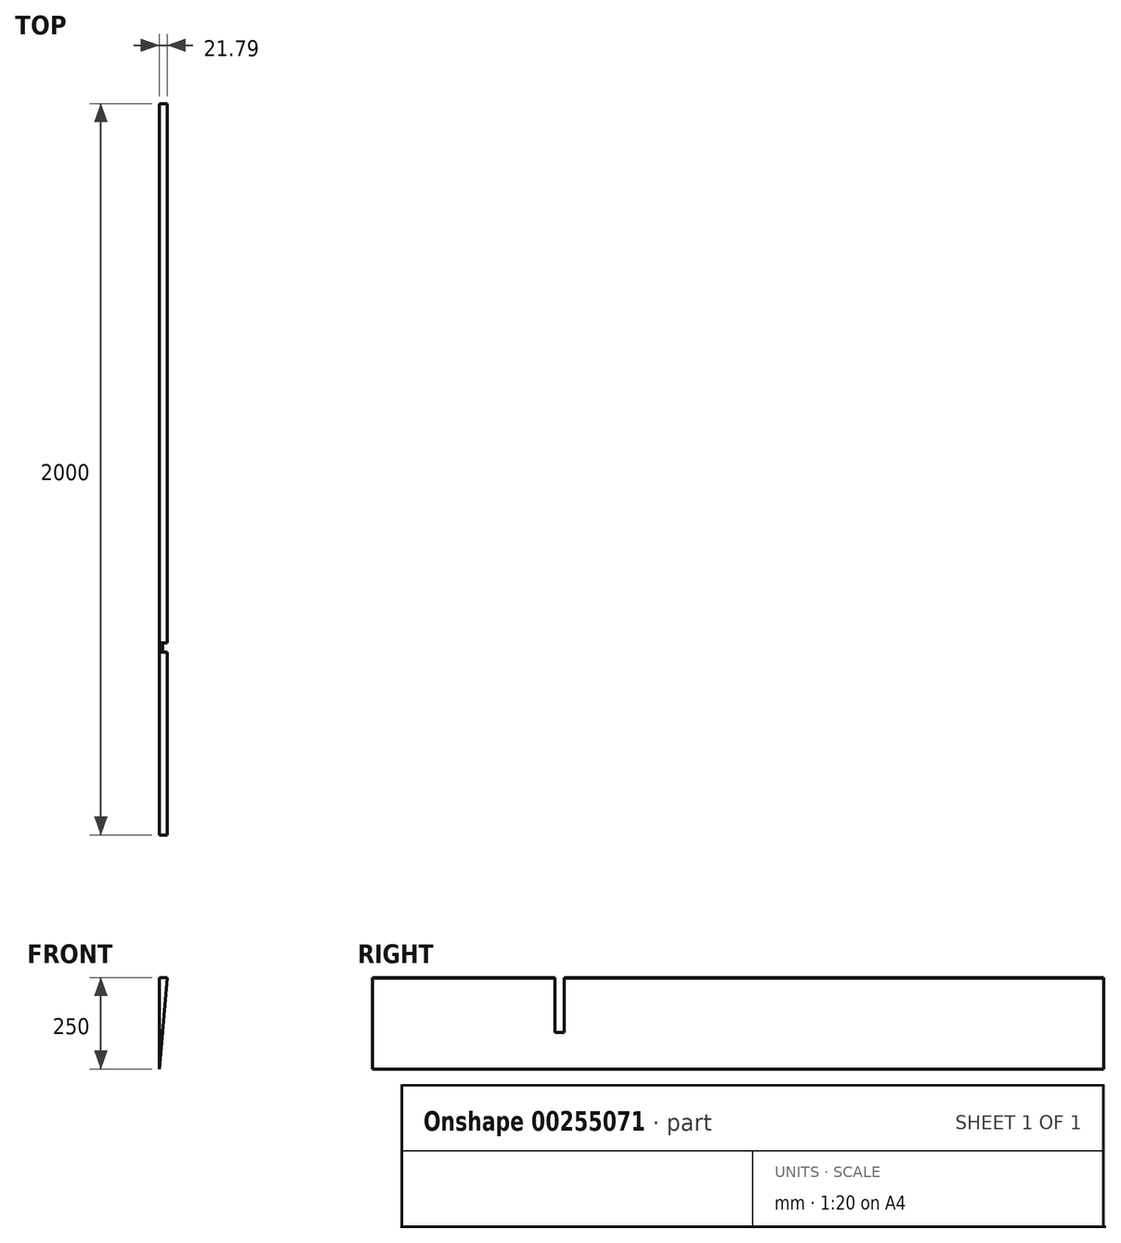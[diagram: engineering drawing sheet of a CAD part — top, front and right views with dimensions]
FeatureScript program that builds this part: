
annotation { "Feature Type Name" : "Feature", "Feature Type Description" : "" }
export const myFeature = defineFeature(function(context is Context, id is Id, definition is map)
    precondition{}
    {
        {
            var Q0;
            Q0=qCreatedBy(makeId("Front.planeOp"),FACE);
            var sketch = newSketch(context, id + "F0", { "sketchPlane" : qUnion([Q0])});
            skCircle(sketch, "E0", {"center": v(0, 0) * mm, "radius": 250 * mm});
            skSolve(sketch);
        }
        {
            var Q0;
            Q0=makeQuery(id+"F0.imprint","IMPRINT",FACE,{"disambiguationData":[TD([[makeQuery(id+"F0.imprint","IMPRINT",EDGE,{"derivedFrom":sQuery(id+"F0.wireOp",EDGE,"E0")}),1.0]])]});
            var sketch = newSketch(context, id + "F1", { "sketchPlane" : qUnion([Q0])});
            skLineSegment(sketch, "E1.bottom", {"start": v(100, -100) * mm, "end": v(-100, -100) * mm});
            skLineSegment(sketch, "E1.top", {"start": v(100, 100) * mm, "end": v(-100, 100) * mm});
            skLineSegment(sketch, "E1.left", {"start": v(100, -100) * mm, "end": v(100, 100) * mm});
            skLineSegment(sketch, "E1.right", {"start": v(-100, -100) * mm, "end": v(-100, 100) * mm});
            skPoint(sketch, "E1.middle", {"position": v(0, 0) * mm});
            skLineSegment(sketch, "E2.bottom", {"start": v(-479.7, 329.5) * mm, "end": v(479.7, 329.5) * mm});
            skLineSegment(sketch, "E2.top", {"start": v(-479.7, -329.5) * mm, "end": v(479.7, -329.5) * mm});
            skLineSegment(sketch, "E2.left", {"start": v(-479.7, 329.5) * mm, "end": v(-479.7, -329.5) * mm});
            skLineSegment(sketch, "E2.right", {"start": v(479.7, 329.5) * mm, "end": v(479.7, -329.5) * mm});
            skSolve(sketch);
        }
        {
            var Q0;
            Q0=makeQuery(id+"F0.imprint","IMPRINT",FACE,{"disambiguationData":[TD([[makeQuery(id+"F0.imprint","IMPRINT",EDGE,{"derivedFrom":sQuery(id+"F0.wireOp",EDGE,"E0")}),1.0]])]});
            extrude(context, id + "F2", {"entities" : qUnion([Q0]), "depth" : 500 * mm});
        }
        {
            var Q0;
            Q0=makeQuery(id+"F1.imprint","IMPRINT",FACE,{"disambiguationData":[TD([[makeQuery(id+"F1.imprint","IMPRINT",EDGE,{"derivedFrom":sQuery(id+"F1.wireOp",EDGE,"E1.bottom")}),1.0]])]});
            var Q1;
            Q1=makeQuery(id+"F1.imprint","IMPRINT",FACE,{"disambiguationData":[TD([[makeQuery(id+"F1.imprint","IMPRINT",EDGE,{"derivedFrom":sQuery(id+"F1.wireOp",EDGE,"E1.bottom")}),-1.0]])]});
            extrude(context, id + "F3", {"entities" : qUnion([Q0, Q1]), "operationType" : NewBodyOperationType.ADD, "oppositeDirection" : true, "depth" : 1500 * mm});
        }
        {
            var Q0;
            Q0 = qSketchRegion(id + "F1", true);
            extrude(context, id + "F4", {"entities" : qUnion([Q0]), "operationType" : NewBodyOperationType.REMOVE, "oppositeDirection" : true, "depth" : 25 * mm});
        }
        {
            var Q0;
            Q0=makeQuery(id+"F2.opExtrude","CAP_FACE",FACE,{"disambiguationData":[OSD([sQuery(id+"F0.wireOp",EDGE,"E0")])],"isStart":false});
            var sketch = newSketch(context, id + "F5", { "sketchPlane" : qUnion([Q0])});
            skLineSegment(sketch, "E3", {"start": v(0, 0) * mm, "end": v(0, 250) * mm});
            skLineSegment(sketch, "E4", {"start": v(0, 0) * mm, "end": v(21.87, 250) * mm});
            skLineSegment(sketch, "E5", {"start": v(21.87, 250) * mm, "end": v(0, 250) * mm});
            skSolve(sketch);
        }
        {
            var Q0;
            {var subQ0=sQuery(id+"F5.wireOp",EDGE,"E3");Q0=makeQuery(id+"F5.imprint","IMPRINT",FACE,{"disambiguationData":[TD([[makeQuery(id+"F5.imprint","IMPRINT",EDGE,{"derivedFrom":subQ0}),-1.0]])]});}
            extrude(context, id + "F6", {"entities" : qUnion([Q0]), "operationType" : NewBodyOperationType.INTERSECT, "oppositeDirection" : true, "depth" : 2000 * mm});
        }
    });
